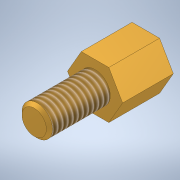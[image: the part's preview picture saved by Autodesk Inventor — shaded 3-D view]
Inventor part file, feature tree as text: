
AUTODESK INVENTOR PART (.ipt)
format: ipt  version: 2022 (Build 260153000, 153)  size: 123,904 bytes
history: native  units: mm
features: sketch x3, extrude x2, thread x1, chamfer x1, hole x1
ambient origin geometry x8: Origin, YZ Plane, XZ Plane, XY Plane, X Axis, Y Axis, Z Axis, Center Point
bodies: Solid1 (feature_tree)
feature tree (8):
  extrude  "Extrusion1"  Depth=5.0mm TaperAngle=0.0deg
  extrude  "Extrusion2"  Depth=6.0mm TaperAngle=0.0deg
  thread  "Thread1"  [1 undecoded]
  chamfer  "Chamfer1"  Distance=0.3mm Angle=45.0deg
  hole  "Hole1"  [1 undecoded]
  sketch  "Sketch1"  dims[d0=4.7mm d1=5.0mm d2=0.0mm]
  sketch  "Sketch2"  dims[d3=3.0mm d4=6.0mm d5=0.0mm d6=6.0mm d7=0.0mm d8=0.3mm d9=2.0mm d10=45.0deg]
  sketch  "Sketch3"  dims[d11=2.459mm d12=4.5mm d13=3.023mm d14=2.0mm d15=14.3117mm d16=4.5mm d17=0.0mm]
note: 2 required parameter values undecoded (feature->parameter linkage not recoverable at this tier; creation-order binding heuristic only, values carry confidence <= 0.55)
